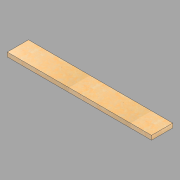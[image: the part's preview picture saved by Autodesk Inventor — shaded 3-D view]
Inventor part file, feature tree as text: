
AUTODESK INVENTOR PART (.ipt)
format: ipt  version: 2022.1 (Build 261234020, 234B)  size: 96,768 bytes
history: native  units: in
note: dims shown in document units (in); Inventor stores cm internally (conversion verified against a paired STEP export)
features: extrude x1, sketch x1
ambient origin geometry x8: Origin, YZ Plane, XZ Plane, XY Plane, X Axis, Y Axis, Z Axis, Center Point
bodies: Solid1 (feature_tree)
feature tree (2):
  extrude  "Extrusion1"  Depth=10.0in
  sketch  "Sketch1"  dims[d0=2.0in d1=10.0in d2=68.125in d3=0.0in]
